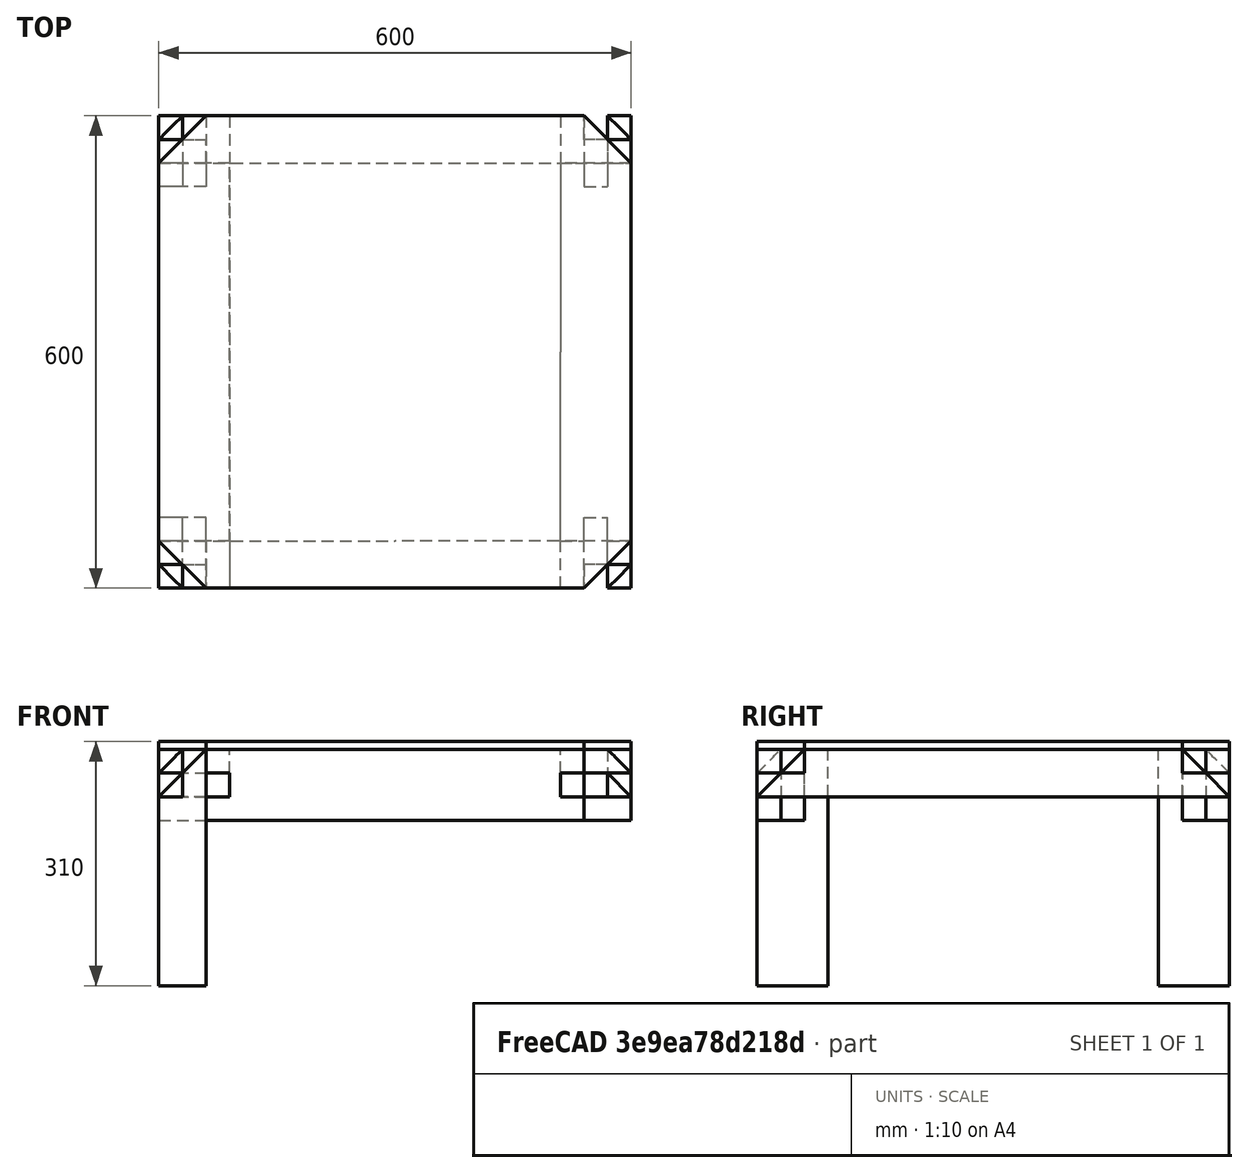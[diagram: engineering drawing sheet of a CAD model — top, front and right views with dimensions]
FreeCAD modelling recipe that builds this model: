
FCSTD DOCUMENT  (FreeCAD 0.18R)
Label: MESA CENTRO
License: All rights reserved
LicenseURL: http://en.wikipedia.org/wiki/All_rights_reserved
objects: Part::Mirroring×10, Part::Feature×8, Part::FeaturePython×8, Part::Box×5, App::DocumentObjectGroup×4, Part::Cut×2, Part::MultiFuse×2, Part::Chamfer×1
note: 36 computed .brp shape members not serialized (recipe doc carries the construction recipe); baked Part::Feature solids carry a one-line shape summary decoded from their .brp

FEATURE [Part::Box] Box  label="Cube"
  AttacherType = Attacher::AttachEngine3D
  Height = 60
  Length = 90
  Width = 300
FEATURE [Part::Box] Box001  label="Cube001"
  AttacherType = Attacher::AttachEngine3D
  Height = 30
  Length = 90
  Placement = pos=(0,0,30) rot=(0,0,1;0rad)
  Width = 60
FEATURE [Part::Cut] Cut
  Base = -> Box
  Tool = -> Box001
FEATURE [Part::Box] Box002  label="Cube002"
  AttacherType = Attacher::AttachEngine3D
  Height = 60
  Length = 30
  Placement = pos=(30,0,0) rot=(0,0,1;0rad)
  Width = 90
FEATURE [Part::Cut] Cut001
  Base = -> Cut
  Tool = -> Box002
FEATURE [Part::Feature] Cut001001  label="Cut002"
  Placement = pos=(30,90,60) rot=(0.57735,-0.57735,0.57735;4.18879rad)
  shape: bbox 60 x 90 x 300 mm, 14 faces (baked)
FEATURE [Part::Feature] Cut001002  label="Cut003"
  Placement = pos=(90,60,-30) rot=(-0.57735,0.57735,-0.57735;4.18879rad)
  shape: bbox 300 x 60 x 90 mm, 14 faces (baked)
FEATURE [Part::Box] Box003  label="Cube003"
  AttacherType = Attacher::AttachEngine3D
  Height = 30
  Length = 30
  Placement = pos=(60,0,30) rot=(0,0,1;0rad)
  Width = 30
FEATURE [Part::Feature] Face
  shape: bbox 99 x 99 x 66 mm, 1 faces, 0 solids (baked)
FEATURE [Part::Feature] Face001
  shape: bbox 99 x 99 x 66 mm, 1 faces, 0 solids (baked)
FEATURE [Part::Feature] Face002
  shape: bbox 99 x 99 x 66 mm, 1 faces, 0 solids (baked)
FEATURE [Part::Feature] Face003
  shape: bbox 99 x 99 x 66 mm, 1 faces, 0 solids (baked)
FEATURE [Part::FeaturePython] Slice  # WARN: FeaturePython — macro-defined, semantics opaque (R4)
  Base = -> Box003
  Mode = 1
  Tolerance = 0
  Tools = -> [Face]
FEATURE [Part::FeaturePython] Slice_child0  label="Slice.0"  # WARN: FeaturePython — macro-defined, semantics opaque (R4)
  Base = -> Slice
  FilterType = 1
  Invert = false
  OverrideMaxVal = 0
  WindowFrom = 80
  WindowTo = 100
  items = 0
FEATURE [App::DocumentObjectGroup] GrExplode_Slice  label="Exploded Slice"
  Group = -> [Slice_child0]
FEATURE [Part::FeaturePython] Slice001  # WARN: FeaturePython — macro-defined, semantics opaque (R4)
  Base = -> Cut001002
  Mode = 1
  Tolerance = 0
  Tools = -> [Face001]
FEATURE [Part::FeaturePython] Slice001_child0  label="Slice001.0"  # WARN: FeaturePython — macro-defined, semantics opaque (R4)
  Base = -> Slice001
  FilterType = 1
  Invert = false
  OverrideMaxVal = 0
  WindowFrom = 80
  WindowTo = 100
  items = 0
FEATURE [Part::FeaturePython] Slice002  # WARN: FeaturePython — macro-defined, semantics opaque (R4)
  Base = -> Cut001001
  Mode = 1
  Tolerance = 0
  Tools = -> [Face002]
FEATURE [Part::FeaturePython] Slice002_child0  label="Slice002.0"  # WARN: FeaturePython — macro-defined, semantics opaque (R4)
  Base = -> Slice002
  FilterType = 1
  Invert = false
  OverrideMaxVal = 0
  WindowFrom = 80
  WindowTo = 100
  items = 0
FEATURE [App::DocumentObjectGroup] GrExplode_Slice002  label="Exploded Slice002"
  Group = -> [Slice002_child0]
FEATURE [Part::FeaturePython] Slice003  # WARN: FeaturePython — macro-defined, semantics opaque (R4)
  Base = -> Cut001
  Mode = 1
  Tolerance = 0
  Tools = -> [Face003]
FEATURE [Part::FeaturePython] Slice003_child0  label="Slice003.0"  # WARN: FeaturePython — macro-defined, semantics opaque (R4)
  Base = -> Slice003
  FilterType = 1
  Invert = false
  OverrideMaxVal = 0
  WindowFrom = 80
  WindowTo = 100
  items = 0
FEATURE [Part::Mirroring] Part__Mirroring  label="Slice003.0 (Mirror #1)"
  Base = (0,300,0)
  Normal = (0,1,0)
  Source = -> Slice003_child0
FEATURE [Part::MultiFuse] Fusion
  Shapes = -> [Slice003_child0,Part__Mirroring]
FEATURE [App::DocumentObjectGroup] GrExplode_Slice003  label="Exploded Slice003"
  Group = -> [Fusion]
FEATURE [Part::Feature] Fusion001
  shape: bbox 125 x 670 x 66 mm, 24 faces (baked)
FEATURE [Part::Mirroring] Part__Mirroring001  label="Slice001.0 (Mirror #2)"
  Base = (-210,0,0)
  Normal = (1,0,0)
  Source = -> Slice001_child0
FEATURE [Part::MultiFuse] Fusion002
  Shapes = -> [Part__Mirroring001,Slice001_child0]
FEATURE [App::DocumentObjectGroup] GrExplode_Slice001  label="Exploded Slice001"
  Group = -> [Fusion002]
FEATURE [Part::Feature] Fusion002001  label="Fusion003"
  shape: bbox 670 x 99 x 92 mm, 24 faces (baked)
FEATURE [Part::Mirroring] Part__Mirroring002  label="Slice.0 (Mirror #3)"
  Base = (0,300,0)
  Normal = (0,1,0)
  Source = -> Slice_child0
FEATURE [Part::Mirroring] Part__Mirroring003  label="Slice002.0 (Mirror #4)"
  Base = (0,300,0)
  Normal = (0,1,0)
  Source = -> Slice002_child0
FEATURE [Part::Mirroring] Part__Mirroring004  label="Fusion003 (Mirror #5)"
  Base = (0,300,0)
  Normal = (0,1,0)
  Source = -> Fusion002001
FEATURE [Part::Mirroring] Part__Mirroring005  label="Slice.0 (Mirror #6)"
  Base = (-210,0,0)
  Normal = (1,0,0)
  Source = -> Slice_child0
FEATURE [Part::Mirroring] Part__Mirroring006  label="Slice002.0 (Mirror #7)"
  Base = (-210,0,0)
  Normal = (1,0,0)
  Source = -> Slice002_child0
FEATURE [Part::Mirroring] Part__Mirroring007  label="Fusion001 (Mirror #8)"
  Base = (-210,0,0)
  Normal = (1,0,0)
  Source = -> Fusion001
FEATURE [Part::Mirroring] Part__Mirroring008  label="Slice.0 (Mirror #9)"
  Base = (-210,0,0)
  Normal = (1,0,0)
  Source = -> Part__Mirroring002
FEATURE [Part::Mirroring] Part__Mirroring009  label="Slice002.0 (Mirror #10)"
  Base = (-210,0,0)
  Normal = (1,0,0)
  Source = -> Part__Mirroring003
FEATURE [Part::Box] Box004  label="Cube004"
  AttacherType = Attacher::AttachEngine3D
  Height = 10
  Length = 600
  Placement = pos=(-510,0,60) rot=(0,0,1;0rad)
  Width = 600
FEATURE [Part::Chamfer] Chamfer
  Base = -> Box004
  Edges = 4 edges r=60: [Edge1,Edge3,Edge5,Edge7]
